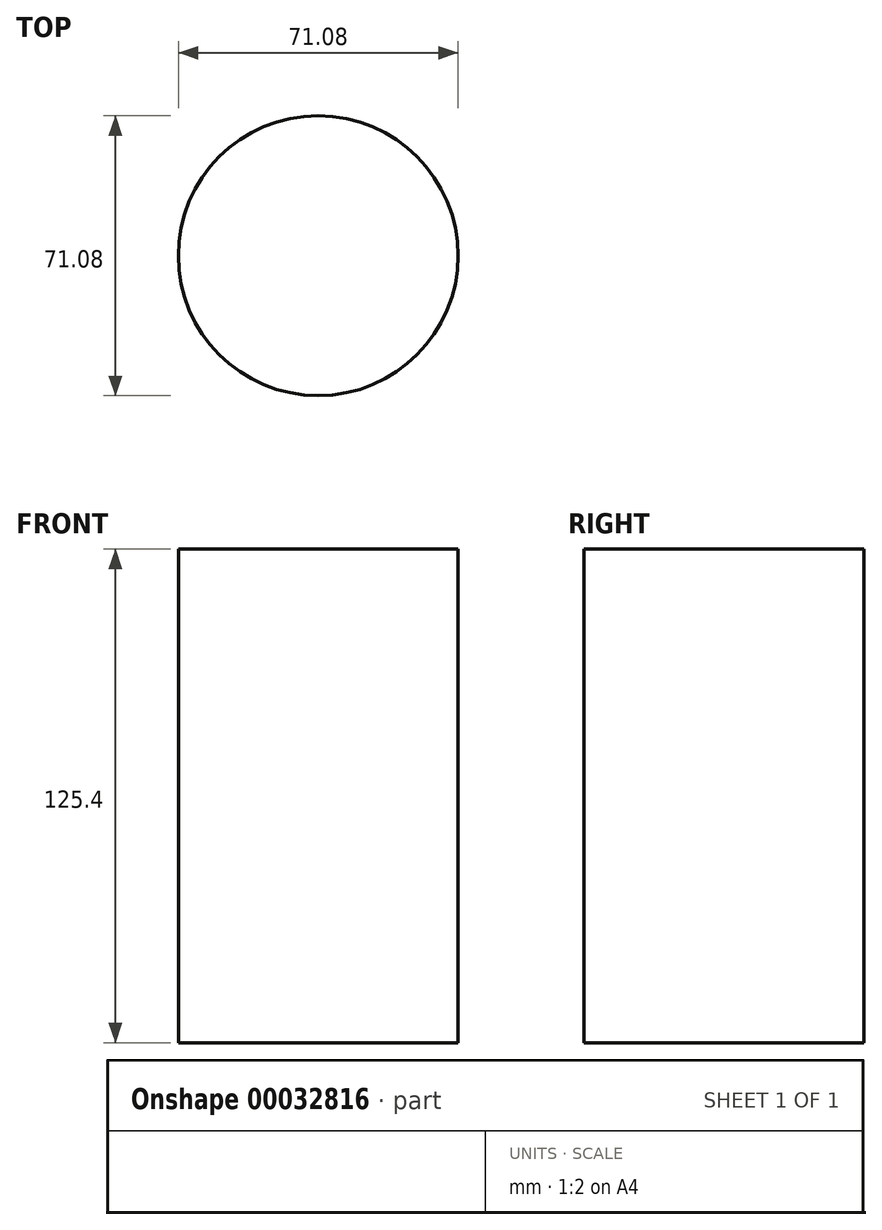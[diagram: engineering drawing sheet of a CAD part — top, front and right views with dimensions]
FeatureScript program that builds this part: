
annotation { "Feature Type Name" : "Feature", "Feature Type Description" : "" }
export const myFeature = defineFeature(function(context is Context, id is Id, definition is map)
    precondition{}
    {
        {
            var Q0;
            Q0=qCreatedBy(makeId("Top.planeOp"),FACE);
            var sketch = newSketch(context, id + "F0", { "sketchPlane" : qUnion([Q0])});
            skCircle(sketch, "E0", {"center": v(0, 0.88) * mm, "radius": 35.54 * mm});
            skSolve(sketch);
        }
        {
            var Q0;
            Q0 = qSketchRegion(id + "F0", true);
            extrude(context, id + "F1", {"entities" : qUnion([Q0]), "depth" : 100 * mm});
        }
        {
            var Q0;
            Q0=makeQuery(id+"F1.opExtrude","CAP_FACE",FACE,{"disambiguationData":[OSD([sQuery(id+"F0.wireOp",EDGE,"E0")])],"isStart":false});
            var sketch = newSketch(context, id + "F2", { "sketchPlane" : qUnion([Q0])});
            skCircle(sketch, "E1", {"center": v(0, 0) * mm, "radius": 16.16 * mm});
            skSolve(sketch);
        }
        {
            var Q0;
            Q0 = qSketchRegion(id + "F2", true);
            extrude(context, id + "F3", {"entities" : qUnion([Q0]), "operationType" : NewBodyOperationType.ADD, "oppositeDirection" : true, "depth" : 25.4 * mm});
        }
        {
            var Q0;
            Q0=makeQuery(id+"F1.opExtrude","CAP_FACE",FACE,{"disambiguationData":[OSD([sQuery(id+"F0.wireOp",EDGE,"E0")])],"isStart":false});
            extrude(context, id + "F4", {"entities" : qUnion([Q0]), "operationType" : NewBodyOperationType.ADD, "depth" : 25.4 * mm});
        }
    });
